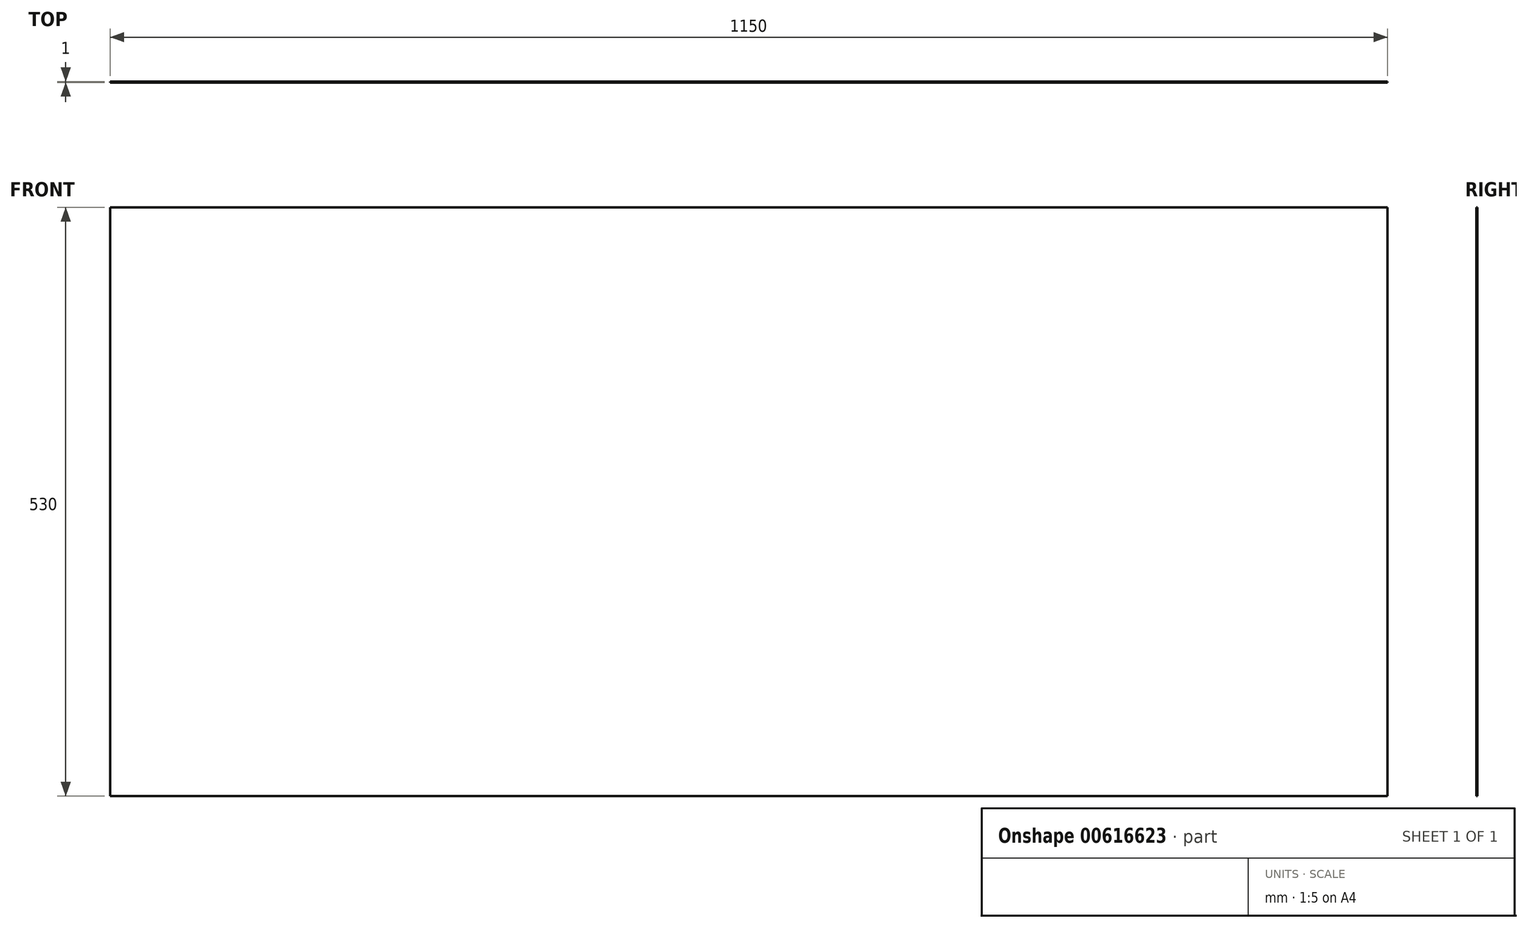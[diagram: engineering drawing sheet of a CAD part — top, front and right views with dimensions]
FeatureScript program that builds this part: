
annotation { "Feature Type Name" : "Feature", "Feature Type Description" : "" }
export const myFeature = defineFeature(function(context is Context, id is Id, definition is map)
    precondition{}
    {
        {
            var Q0;
            Q0=qCreatedBy(makeId("Front.planeOp"),FACE);
            var sketch = newSketch(context, id + "F0", { "sketchPlane" : qUnion([Q0])});
            skLineSegment(sketch, "E0.bottom", {"start": v(-778.37, 293.7) * mm, "end": v(371.63, 293.7) * mm});
            skLineSegment(sketch, "E0.top", {"start": v(-778.37, -236.3) * mm, "end": v(371.63, -236.3) * mm});
            skLineSegment(sketch, "E0.left", {"start": v(-778.37, 293.7) * mm, "end": v(-778.37, -236.3) * mm});
            skLineSegment(sketch, "E0.right", {"start": v(371.63, 293.7) * mm, "end": v(371.63, -236.3) * mm});
            skSolve(sketch);
        }
        {
            var Q0;
            Q0=makeQuery(id+"F0.imprint","IMPRINT",FACE,{"disambiguationData":[TD([[makeQuery(id+"F0.imprint","IMPRINT",EDGE,{"derivedFrom":sQuery(id+"F0.wireOp",EDGE,"E0.bottom")}),-1.0]])]});
            extrude(context, id + "F1", {"entities" : qUnion([Q0]), "depth" : 1 * mm, "offsetDistance" : 25 * mm});
        }
    });
